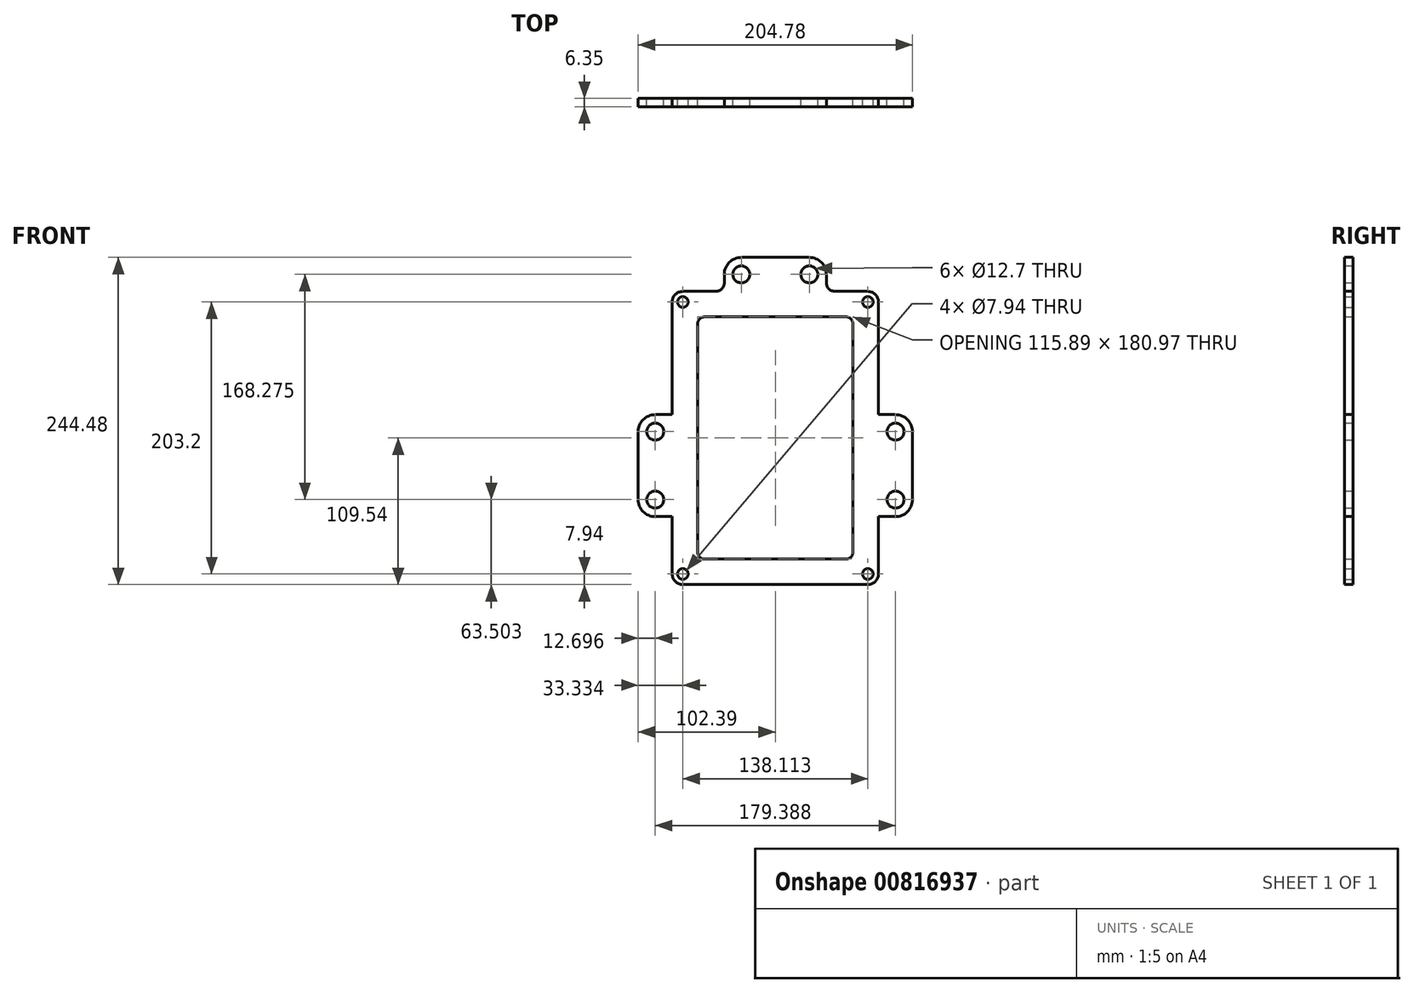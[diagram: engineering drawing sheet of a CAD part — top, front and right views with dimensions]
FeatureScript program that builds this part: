
annotation { "Feature Type Name" : "Feature", "Feature Type Description" : "" }
export const myFeature = defineFeature(function(context is Context, id is Id, definition is map)
    precondition{}
    {
        {
            var Q0;
            Q0=qCreatedBy(makeId("Front.planeOp"),FACE);
            var sketch = newSketch(context, id + "F0", { "sketchPlane" : qUnion([Q0])});
            skCircle(sketch, "E0", {"center": v(0, 0) * mm, "radius": 142.88 * mm, "construction": true});
            skLineSegment(sketch, "E1.bottom", {"start": v(-69.06, 101.6) * mm, "end": v(69.06, 101.6) * mm, "construction": true});
            skLineSegment(sketch, "E1.top", {"start": v(-69.06, -101.6) * mm, "end": v(69.06, -101.6) * mm, "construction": true});
            skLineSegment(sketch, "E1.left", {"start": v(-69.06, 101.6) * mm, "end": v(-69.06, -101.6) * mm, "construction": true});
            skLineSegment(sketch, "E1.right", {"start": v(69.06, 101.6) * mm, "end": v(69.06, -101.6) * mm, "construction": true});
            skCircle(sketch, "E2", {"center": v(-69.06, 101.6) * mm, "radius": 3.97 * mm});
            skCircle(sketch, "E3", {"center": v(-69.06, -101.6) * mm, "radius": 3.97 * mm});
            skCircle(sketch, "E4", {"center": v(69.06, -101.6) * mm, "radius": 3.97 * mm});
            skCircle(sketch, "E5", {"center": v(69.06, 101.6) * mm, "radius": 3.97 * mm});
            skArc(sketch, "E6.0", {"start": v(-69.06, 109.54) * mm, "mid": v(-74.67, 107.21) * mm, "end": v(-77, 101.6) * mm});
            skArc(sketch, "E7.0", {"start": v(-77, -101.6) * mm, "mid": v(-74.67, -107.21) * mm, "end": v(-69.06, -109.54) * mm});
            skArc(sketch, "E8.0", {"start": v(77, 101.6) * mm, "mid": v(74.67, 107.21) * mm, "end": v(69.06, 109.54) * mm});
            skArc(sketch, "E9.0", {"start": v(69.06, -109.54) * mm, "mid": v(74.67, -107.21) * mm, "end": v(77, -101.6) * mm});
            skLineSegment(sketch, "E10", {"start": v(-77, 101.6) * mm, "end": v(-77, 17.46) * mm});
            skLineSegment(sketch, "E11", {"start": v(-69.06, -109.54) * mm, "end": v(69.06, -109.54) * mm});
            skLineSegment(sketch, "E12", {"start": v(77, -101.6) * mm, "end": v(77, -58.74) * mm});
            skLineSegment(sketch, "E13", {"start": v(69.06, 109.54) * mm, "end": v(44.45, 109.54) * mm});
            skLineSegment(sketch, "E14.bottom", {"start": v(-57.94, 90.49) * mm, "end": v(57.94, 90.49) * mm});
            skLineSegment(sketch, "E14.top", {"start": v(-57.94, -90.49) * mm, "end": v(57.94, -90.49) * mm});
            skLineSegment(sketch, "E14.left", {"start": v(-57.94, 90.49) * mm, "end": v(-57.94, -90.49) * mm});
            skLineSegment(sketch, "E14.right", {"start": v(57.94, 90.49) * mm, "end": v(57.94, -90.49) * mm});
            skLineSegment(sketch, "E15.top", {"start": v(-25.4, 134.94) * mm, "end": v(25.4, 134.94) * mm});
            skLineSegment(sketch, "E15.left", {"start": v(-38.1, 115.89) * mm, "end": v(-38.1, 122.24) * mm});
            skLineSegment(sketch, "E15.right", {"start": v(38.1, 115.89) * mm, "end": v(38.1, 122.24) * mm});
            skLineSegment(sketch, "E16", {"start": v(-38.1, 122.24) * mm, "end": v(38.1, 122.24) * mm, "construction": true});
            skCircle(sketch, "E17", {"center": v(-25.4, 122.24) * mm, "radius": 6.35 * mm});
            skCircle(sketch, "E18", {"center": v(25.4, 122.24) * mm, "radius": 6.35 * mm});
            skArc(sketch, "E19", {"start": v(-25.4, 134.94) * mm, "mid": v(-34.38, 131.22) * mm, "end": v(-38.1, 122.24) * mm});
            skArc(sketch, "E20", {"start": v(38.1, 122.24) * mm, "mid": v(34.38, 131.22) * mm, "end": v(25.4, 134.94) * mm});
            skPoint(sketch, "E21.orphan", {"position": v(38.1, 134.94) * mm});
            skPoint(sketch, "E22.orphan", {"position": v(-38.1, 134.94) * mm});
            skLineSegment(sketch, "E23.trimOffspring", {"start": v(-44.45, 109.54) * mm, "end": v(-69.06, 109.54) * mm});
            skPoint(sketch, "E24.visualSharp", {"position": v(-38.1, 109.54) * mm});
            skArc(sketch, "E24.filletArc", {"start": v(-44.45, 109.54) * mm, "mid": v(-39.96, 111.4) * mm, "end": v(-38.1, 115.89) * mm});
            skPoint(sketch, "E25.visualSharp", {"position": v(38.1, 109.54) * mm});
            skArc(sketch, "E25.filletArc", {"start": v(38.1, 115.89) * mm, "mid": v(39.96, 111.4) * mm, "end": v(44.45, 109.54) * mm});
            skLineSegment(sketch, "E26.bottom", {"start": v(-89.7, 17.46) * mm, "end": v(-77, 17.46) * mm});
            skLineSegment(sketch, "E26.top", {"start": v(-89.7, -58.74) * mm, "end": v(-77, -58.74) * mm});
            skLineSegment(sketch, "E26.left", {"start": v(-102.4, 4.76) * mm, "end": v(-102.4, -46.04) * mm});
            skLineSegment(sketch, "E27", {"start": v(-89.7, 17.46) * mm, "end": v(-89.7, -58.74) * mm, "construction": true});
            skCircle(sketch, "E28", {"center": v(-89.7, -46.04) * mm, "radius": 6.35 * mm});
            skCircle(sketch, "E29", {"center": v(-89.7, 4.76) * mm, "radius": 6.35 * mm});
            skArc(sketch, "E30", {"start": v(-89.7, 17.46) * mm, "mid": v(-98.67, 13.74) * mm, "end": v(-102.4, 4.76) * mm});
            skArc(sketch, "E31", {"start": v(-102.4, -46.04) * mm, "mid": v(-98.67, -55.02) * mm, "end": v(-89.7, -58.74) * mm});
            skPoint(sketch, "E32.orphan", {"position": v(-102.4, -58.74) * mm});
            skPoint(sketch, "E33.orphan", {"position": v(-102.4, 17.46) * mm});
            skCircle(sketch, "E34.MirrorC", {"center": v(89.7, -46.04) * mm, "radius": 6.35 * mm});
            skCircle(sketch, "E35.MirrorC", {"center": v(89.7, 4.76) * mm, "radius": 6.35 * mm});
            skLineSegment(sketch, "E36.MirrorCS", {"start": v(102.4, 4.76) * mm, "end": v(102.4, -46.04) * mm});
            skArc(sketch, "E37.MirrorCS", {"start": v(102.4, -46.04) * mm, "mid": v(98.67, -55.02) * mm, "end": v(89.7, -58.74) * mm});
            skLineSegment(sketch, "E38.MirrorCS", {"start": v(89.7, -58.74) * mm, "end": v(77, -58.74) * mm});
            skLineSegment(sketch, "E39.MirrorCS", {"start": v(89.7, 17.46) * mm, "end": v(77, 17.46) * mm});
            skArc(sketch, "E40.MirrorCS", {"start": v(89.7, 17.46) * mm, "mid": v(98.67, 13.74) * mm, "end": v(102.4, 4.76) * mm});
            skLineSegment(sketch, "E41.trimOffspring", {"start": v(77, 17.46) * mm, "end": v(77, 101.6) * mm});
            skLineSegment(sketch, "E42.trimOffspring", {"start": v(-77, -58.74) * mm, "end": v(-77, -101.6) * mm});
            skSolve(sketch);
        }
        {
            var Q0;
            Q0 = qSketchRegion(id + "F0", true);
            extrude(context, id + "F1", {"entities" : qUnion([Q0]), "depth" : 6.35 * mm, "offsetDistance" : 25.4 * mm});
        }
        {
            var Q0;
            Q0=makeQuery(id+"F1.opExtrude","SWEPT_EDGE",EDGE,{"disambiguationData":[OSD([sQuery(id+"F0.wireOp",EDGE,"E14.bottom"),sQuery(id+"F0.wireOp",EDGE,"E14.left")])]});
            var Q1;
            Q1=makeQuery(id+"F1.opExtrude","SWEPT_EDGE",EDGE,{"disambiguationData":[OSD([sQuery(id+"F0.wireOp",EDGE,"E14.bottom"),sQuery(id+"F0.wireOp",EDGE,"E14.right")])]});
            var Q2;
            Q2=makeQuery(id+"F1.opExtrude","SWEPT_EDGE",EDGE,{"disambiguationData":[OSD([sQuery(id+"F0.wireOp",EDGE,"E14.top"),sQuery(id+"F0.wireOp",EDGE,"E14.right")])]});
            var Q3;
            Q3=makeQuery(id+"F1.opExtrude","SWEPT_EDGE",EDGE,{"disambiguationData":[OSD([sQuery(id+"F0.wireOp",EDGE,"E14.top"),sQuery(id+"F0.wireOp",EDGE,"E14.left")])]});
            fillet(context, id + "F2", {"entities" : qUnion([Q0, Q1, Q2, Q3]), "radius" : 5.08 * mm, "tangentPropagation" : true, "allowEdgeOverflow" : false});
        }
    });
